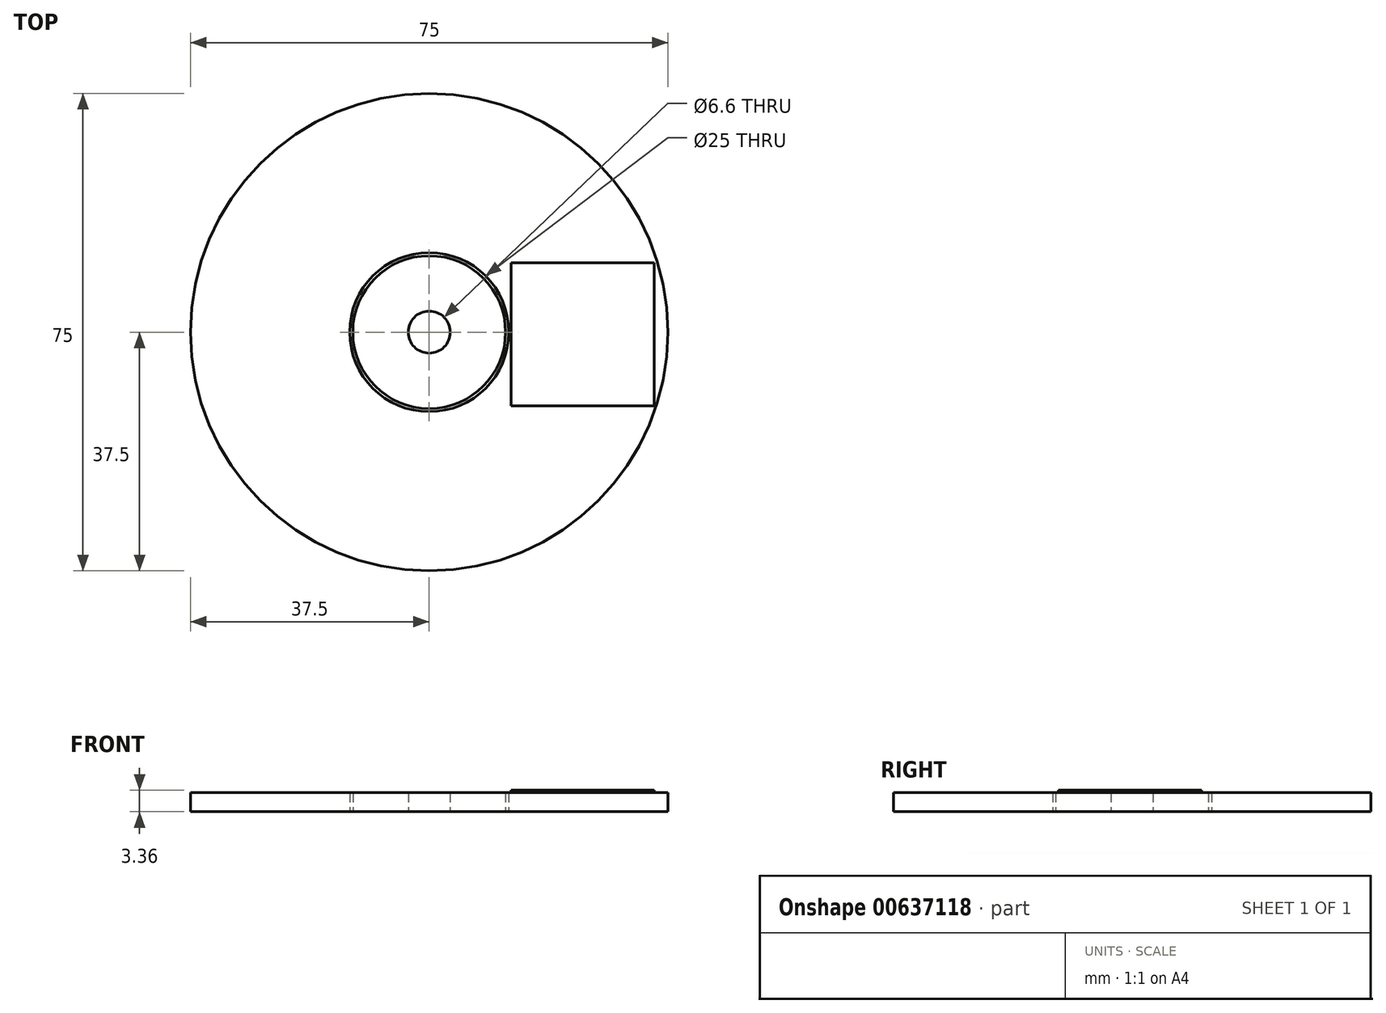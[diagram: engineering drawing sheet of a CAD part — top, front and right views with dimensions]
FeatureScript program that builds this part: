
annotation { "Feature Type Name" : "Feature", "Feature Type Description" : "" }
export const myFeature = defineFeature(function(context is Context, id is Id, definition is map)
    precondition{}
    {
        {
            var Q0;
            Q0=qCreatedBy(makeId("Top.planeOp"),FACE);
            var sketch = newSketch(context, id + "F0", { "sketchPlane" : qUnion([Q0])});
            skCircle(sketch, "E0", {"center": v(0, 0) * mm, "radius": 37.5 * mm});
            skCircle(sketch, "E1", {"center": v(0, 0) * mm, "radius": 12.5 * mm});
            skSolve(sketch);
        }
        {
            var Q0;
            Q0 = qSketchRegion(id + "F0", true);
            extrude(context, id + "F1", {"entities" : qUnion([Q0]), "depth" : 3 * mm, "offsetDistance" : 25 * mm});
        }
        {
            var Q0;
            Q0=qCreatedBy(makeId("Top.planeOp"),FACE);
            var sketch = newSketch(context, id + "F2", { "sketchPlane" : qUnion([Q0])});
            skCircle(sketch, "E2", {"center": v(0, 0) * mm, "radius": 12 * mm});
            skCircle(sketch, "E3", {"center": v(0, 0) * mm, "radius": 3.3 * mm});
            skSolve(sketch);
        }
        {
            var Q0;
            Q0 = qSketchRegion(id + "F2", true);
            extrude(context, id + "F3", {"entities" : qUnion([Q0]), "depth" : 3 * mm, "offsetDistance" : 25 * mm});
        }
        {
            var Q0;
            Q0=makeQuery(id+"F1.opExtrude","CAP_FACE",FACE,{"disambiguationData":[OSD([sQuery(id+"F0.wireOp",EDGE,"E0"),sQuery(id+"F0.wireOp",EDGE,"E1")])],"isStart":false});
            var sketch = newSketch(context, id + "F4", { "sketchPlane" : qUnion([Q0])});
            skLineSegment(sketch, "E4.bottom", {"start": v(12.83, -11.59) * mm, "end": v(35.33, -11.59) * mm});
            skLineSegment(sketch, "E4.top", {"start": v(12.83, 10.91) * mm, "end": v(35.33, 10.91) * mm});
            skLineSegment(sketch, "E4.left", {"start": v(12.83, -11.59) * mm, "end": v(12.83, 10.91) * mm});
            skLineSegment(sketch, "E4.right", {"start": v(35.33, -11.59) * mm, "end": v(35.33, 10.91) * mm});
            skSolve(sketch);
        }
        {
            var Q0;
            Q0 = qSketchRegion(id + "F4", true);
            extrude(context, id + "F5", {"entities" : qUnion([Q0]), "depth" : 0.36 * mm, "offsetDistance" : 25 * mm});
        }
    });
